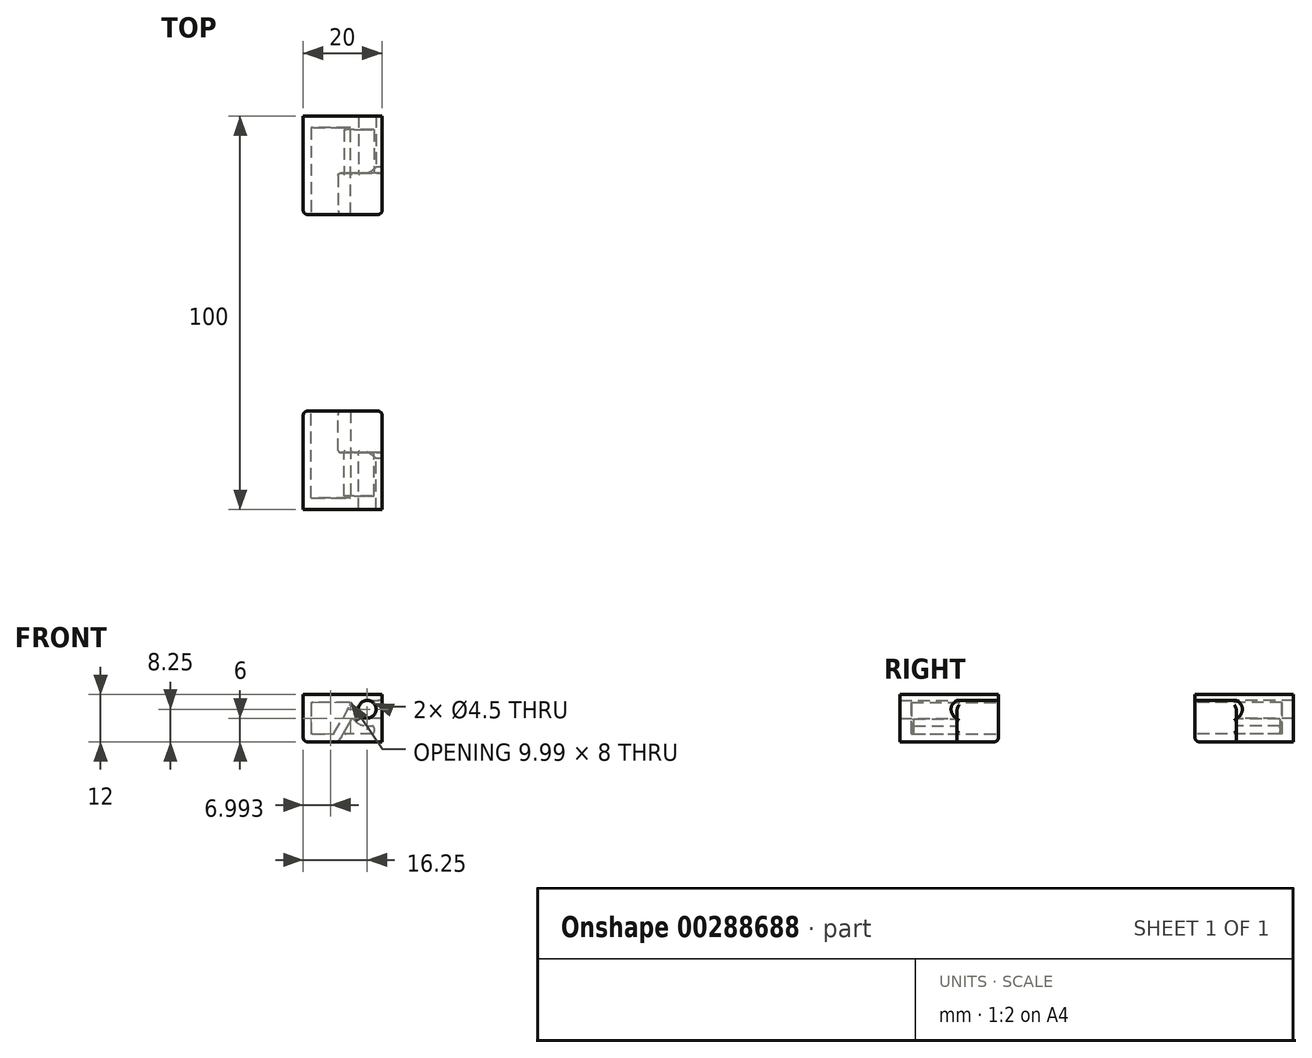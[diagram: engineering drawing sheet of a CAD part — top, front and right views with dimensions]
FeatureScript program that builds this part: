
annotation { "Feature Type Name" : "Feature", "Feature Type Description" : "" }
export const myFeature = defineFeature(function(context is Context, id is Id, definition is map)
    precondition{}
    {
        {
            var Q0;
            Q0=qCreatedBy(makeId("Front.planeOp"),FACE);
            var sketch = newSketch(context, id + "F0", { "sketchPlane" : qUnion([Q0])});
            skCircle(sketch, "E0", {"center": v(0, 0) * mm, "radius": 2.25 * mm});
            skLineSegment(sketch, "E1.bottom", {"start": v(-16.25, 3.75) * mm, "end": v(3.75, 3.75) * mm});
            skLineSegment(sketch, "E1.top", {"start": v(-16.25, -8.25) * mm, "end": v(3.75, -8.25) * mm});
            skLineSegment(sketch, "E1.left", {"start": v(-16.25, 3.75) * mm, "end": v(-16.25, -8.25) * mm});
            skLineSegment(sketch, "E1.right", {"start": v(3.75, 3.75) * mm, "end": v(3.75, -8.25) * mm});
            skSolve(sketch);
        }
        {
            var Q0;
            Q0=makeQuery(id+"F0.imprint","IMPRINT",FACE,{"disambiguationData":[TD([[makeQuery(id+"F0.imprint","IMPRINT",EDGE,{"derivedFrom":sQuery(id+"F0.wireOp",EDGE,"E0")}),-1.0]])]});
            extrude(context, id + "F1", {"entities" : qUnion([Q0]), "oppositeDirection" : true, "depth" : 25 * mm});
        }
        {
            var Q0;
            Q0=makeQuery(id+"F1.opExtrude","CAP_FACE",FACE,{"disambiguationData":[OSD([sQuery(id+"F0.wireOp",EDGE,"E0"),sQuery(id+"F0.wireOp",EDGE,"E1.bottom"),sQuery(id+"F0.wireOp",EDGE,"E1.top"),sQuery(id+"F0.wireOp",EDGE,"E1.left"),sQuery(id+"F0.wireOp",EDGE,"E1.right")])],"isStart":true});
            var sketch = newSketch(context, id + "F2", { "sketchPlane" : qUnion([Q0])});
            skLineSegment(sketch, "E2", {"start": v(0, 2.25) * mm, "end": v(3.75, 2.25) * mm});
            skLineSegment(sketch, "E3", {"start": v(-1.95, 1.13) * mm, "end": v(-7.36, -8.25) * mm});
            skArc(sketch, "E4.0", {"start": v(0, 2.25) * mm, "mid": v(-1.13, 1.95) * mm, "end": v(-1.95, 1.13) * mm});
            skPoint(sketch, "E5.orphan", {"position": v(3.75, -8.25) * mm});
            skLineSegment(sketch, "E6.0", {"start": v(-7.36, -8.25) * mm, "end": v(3.75, -8.25) * mm});
            skLineSegment(sketch, "E7.0", {"start": v(3.75, 2.25) * mm, "end": v(3.75, -8.25) * mm});
            skPoint(sketch, "E8.orphan", {"position": v(3.75, 3.75) * mm});
            skPoint(sketch, "E9.orphan", {"position": v(-16.25, -8.25) * mm});
            skSolve(sketch);
        }
        {
            var Q0;
            Q0 = qSketchRegion(id + "F2", true);
            extrude(context, id + "F3", {"entities" : qUnion([Q0]), "operationType" : NewBodyOperationType.REMOVE, "oppositeDirection" : true, "depth" : 10.5 * mm});
        }
        {
            var Q0;
            Q0=makeQuery(id+"F1.opExtrude","CAP_FACE",FACE,{"disambiguationData":[OSD([sQuery(id+"F0.wireOp",EDGE,"E0"),sQuery(id+"F0.wireOp",EDGE,"E1.bottom"),sQuery(id+"F0.wireOp",EDGE,"E1.top"),sQuery(id+"F0.wireOp",EDGE,"E1.left"),sQuery(id+"F0.wireOp",EDGE,"E1.right")])],"isStart":true});
            var sketch = newSketch(context, id + "F4", { "sketchPlane" : qUnion([Q0])});
            skLineSegment(sketch, "E10", {"start": v(-14.25, 1.75) * mm, "end": v(-14.25, -6.25) * mm});
            skLineSegment(sketch, "E11", {"start": v(-14.25, -6.25) * mm, "end": v(-8.52, -6.25) * mm});
            skLineSegment(sketch, "E12", {"start": v(-8.52, -6.25) * mm, "end": v(-3.9, 1.75) * mm});
            skLineSegment(sketch, "E13", {"start": v(-3.9, 1.75) * mm, "end": v(-14.25, 1.75) * mm});
            skSolve(sketch);
        }
        {
            var Q0;
            Q0 = qSketchRegion(id + "F4", true);
            extrude(context, id + "F5", {"entities" : qUnion([Q0]), "operationType" : NewBodyOperationType.REMOVE, "oppositeDirection" : true, "depth" : 22 * mm});
        }
        {
            var Q0;
            Q0=makeQuery(id+"F3.boolean.opBoolean","COPY",FACE,{"derivedFrom":makeQuery(id+"F3.opExtrude","CAP_FACE",FACE,{"disambiguationData":[OSD([sQuery(id+"F2.wireOp",EDGE,"E2"),sQuery(id+"F2.wireOp",EDGE,"E3"),sQuery(id+"F2.wireOp",EDGE,"E4.0"),sQuery(id+"F2.wireOp",EDGE,"E6.0"),sQuery(id+"F2.wireOp",EDGE,"E7.0")])],"isStart":false})});
            var sketch = newSketch(context, id + "F6", { "sketchPlane" : qUnion([Q0])});
            skLineSegment(sketch, "E14.0.1", {"start": v(-3.75, -2) * mm, "end": v(-6.2, -6.25) * mm});
            skArc(sketch, "E15.trimOffspring", {"start": v(-3.75, -2) * mm, "mid": v(-2.19, -3.64) * mm, "end": v(0, -4.25) * mm});
            skPoint(sketch, "E14.0.0.start.orphan", {"position": v(0, 2.25) * mm});
            skPoint(sketch, "E14.0.4.start.orphan", {"position": v(3.75, 2.25) * mm});
            skPoint(sketch, "E16.orphan", {"position": v(-1.95, 1.13) * mm});
            skPoint(sketch, "E17.0.2.end.orphan", {"position": v(3.75, -8.25) * mm});
            skPoint(sketch, "E17.0.2.start.orphan", {"position": v(-7.36, -8.25) * mm});
            skLineSegment(sketch, "E18", {"start": v(0, -4.25) * mm, "end": v(1.75, -4.25) * mm});
            skLineSegment(sketch, "E19", {"start": v(1.75, -4.25) * mm, "end": v(1.75, -6.25) * mm});
            skLineSegment(sketch, "E20", {"start": v(1.75, -6.25) * mm, "end": v(-6.2, -6.25) * mm});
            skSolve(sketch);
        }
        {
            var Q0;
            Q0 = qSketchRegion(id + "F6", true);
            extrude(context, id + "F7", {"entities" : qUnion([Q0]), "operationType" : NewBodyOperationType.REMOVE, "oppositeDirection" : true, "depth" : 11 * mm});
        }
        {
            var Q0;
            Q0=qCreatedBy(makeId("Right.planeOp"),FACE);
            var sketch = newSketch(context, id + "F8", { "sketchPlane" : qUnion([Q0])});
            skArc(sketch, "E21", {"start": v(10.5, -2.25) * mm, "mid": v(12, 0) * mm, "end": v(10.5, 2.25) * mm});
            skLineSegment(sketch, "E22", {"start": v(10.5, 2.25) * mm, "end": v(10.5, -2.25) * mm});
            skSolve(sketch);
        }
        {
            var Q0;
            Q0 = qSketchRegion(id + "F8", true);
            extrude(context, id + "F9", {"entities" : qUnion([Q0]), "operationType" : NewBodyOperationType.REMOVE, "endBound" : BoundingType.THROUGH_ALL, "depth" : 25 * mm});
        }
        {
            var Q0;
            Q0=makeQuery(id+"F1.opExtrude","SWEPT_FACE",FACE,{"disambiguationData":[OSD([sQuery(id+"F0.wireOp",EDGE,"E0")])]});
            var Q1;
            Q1=makeQuery(id+"F3.boolean.opBoolean","COPY",EDGE,{"derivedFrom":makeQuery(id+"F3.opExtrude","CAP_EDGE",EDGE,{"disambiguationData":[OSD([sQuery(id+"F2.wireOp",EDGE,"E3")])],"isStart":true})});
            cPlane(context, id + "F10", {"entities" : qUnion([Q0, Q1]), "cplaneType" : CPlaneType.LINE_ANGLE, "offset" : 25 * mm, "angle" : 90 * degree, "oppositeDirection" : true, "width" : 150 * mm, "height" : 150 * mm});
        }
        {
            var Q0;
            Q0=qCreatedBy(id+"F10.planeOp",FACE);
            var sketch = newSketch(context, id + "F11", { "sketchPlane" : qUnion([Q0])});
            skLineSegment(sketch, "E23", {"start": v(0, 1.94) * mm, "end": v(0, -15.89) * mm, "construction": true});
            skArc(sketch, "E24", {"start": v(-2.25, -10.5) * mm, "mid": v(0, -12) * mm, "end": v(2.25, -10.5) * mm});
            skLineSegment(sketch, "E25", {"start": v(-2.25, -10.5) * mm, "end": v(2.25, -10.5) * mm});
            skSolve(sketch);
        }
        {
            var Q0;
            Q0=makeQuery(id+"F11.imprint","IMPRINT",FACE,{"disambiguationData":[TD([[makeQuery(id+"F11.imprint","IMPRINT",EDGE,{"derivedFrom":sQuery(id+"F11.wireOp",EDGE,"E24")}),1.0]])]});
            extrude(context, id + "F12", {"entities" : qUnion([Q0]), "operationType" : NewBodyOperationType.REMOVE, "endBound" : BoundingType.THROUGH_ALL, "depth" : 25 * mm});
        }
        {
            var Q0;
            Q0=makeQuery(id+"F5.boolean.opBoolean","COPY",EDGE,{"derivedFrom":makeQuery(id+"F5.opExtrude","SWEPT_EDGE",EDGE,{"disambiguationData":[OSD([sQuery(id+"F4.wireOp",EDGE,"E10"),sQuery(id+"F4.wireOp",EDGE,"E13")])]})});
            var Q1;
            Q1=makeQuery(id+"F5.boolean.opBoolean","COPY",EDGE,{"derivedFrom":makeQuery(id+"F5.opExtrude","SWEPT_EDGE",EDGE,{"disambiguationData":[OSD([sQuery(id+"F4.wireOp",EDGE,"E12"),sQuery(id+"F4.wireOp",EDGE,"E13")])]})});
            var Q2;
            Q2=makeQuery(id+"F5.boolean.opBoolean","COPY",EDGE,{"derivedFrom":makeQuery(id+"F5.opExtrude","SWEPT_EDGE",EDGE,{"disambiguationData":[OSD([sQuery(id+"F4.wireOp",EDGE,"E10"),sQuery(id+"F4.wireOp",EDGE,"E11")])]})});
            var Q3;
            Q3=makeQuery(id+"F5.boolean.opBoolean","COPY",EDGE,{"derivedFrom":makeQuery(id+"F5.opExtrude","SWEPT_EDGE",EDGE,{"disambiguationData":[OSD([sQuery(id+"F4.wireOp",EDGE,"E11"),sQuery(id+"F4.wireOp",EDGE,"E12")])]})});
            var Q4;
            Q4=makeQuery(id+"F7.boolean.opBoolean","COPY",EDGE,{"derivedFrom":makeQuery(id+"F7.opExtrude","SWEPT_EDGE",EDGE,{"disambiguationData":[OSD([sQuery(id+"F2.wireOp",EDGE,"E3"),sQuery(id+"F6.wireOp",EDGE,"E14.0.1"),sQuery(id+"F6.wireOp",EDGE,"CT78Zgtt-ATp1-XAIS-9uUU-WfGeracGuKnf")])]})});
            var Q5;
            Q5=makeQuery(id+"F7.boolean.opBoolean","COPY",EDGE,{"derivedFrom":makeQuery(id+"F7.opExtrude","SWEPT_EDGE",EDGE,{"disambiguationData":[OSD([sQuery(id+"F2.wireOp",EDGE,"E3"),sQuery(id+"F6.wireOp",EDGE,"E14.0.1"),sQuery(id+"F6.wireOp",EDGE,"E15.trimOffspring")])]})});
            var Q6;
            Q6=makeQuery(id+"F7.boolean.opBoolean","COPY",EDGE,{"derivedFrom":makeQuery(id+"F7.opExtrude","SWEPT_EDGE",EDGE,{"disambiguationData":[OSD([sQuery(id+"F6.wireOp",EDGE,"E19"),sQuery(id+"F6.wireOp",EDGE,"E20")])]})});
            var Q7;
            Q7=makeQuery(id+"F7.boolean.opBoolean","COPY",EDGE,{"derivedFrom":makeQuery(id+"F7.opExtrude","SWEPT_EDGE",EDGE,{"disambiguationData":[OSD([sQuery(id+"F6.wireOp",EDGE,"E18"),sQuery(id+"F6.wireOp",EDGE,"E19")])]})});
            var Q8;
            {var subQ0=sQuery(id+"F11.wireOp",EDGE,"E24");var subQ1=sQuery(id+"F11.wireOp",EDGE,"E25");Q8=makeQuery(id+"F12.boolean.opBoolean","COPY",EDGE,{"disambiguationData":[TD([makeQuery(id+"F1.opExtrude","SWEPT_FACE",FACE,{"disambiguationData":[OSD([sQuery(id+"F0.wireOp",EDGE,"E1.top")])]})])],"derivedFrom":makeQuery(id+"F12.opExtrude","SWEPT_EDGE",EDGE,{"disambiguationData":[OSD([subQ0,subQ1]),TDD([makeQuery(id+"F11.imprint","INTERSECT",VERTEX,{"disambiguationData":[OD(1.0)],"derivedFrom":[subQ0,subQ1]})])]})});}
            var Q9;
            {var subQ0=sQuery(id+"F11.wireOp",EDGE,"E24");var subQ1=sQuery(id+"F11.wireOp",EDGE,"E25");Q9=makeQuery(id+"F12.boolean.opBoolean","COPY",EDGE,{"disambiguationData":[TD([makeQuery(id+"F7.boolean.opBoolean","COPY",FACE,{"derivedFrom":makeQuery(id+"F7.opExtrude","SWEPT_FACE",FACE,{"disambiguationData":[OSD([sQuery(id+"F6.wireOp",EDGE,"E18")])]})})])],"derivedFrom":makeQuery(id+"F12.opExtrude","SWEPT_EDGE",EDGE,{"disambiguationData":[OSD([subQ0,subQ1]),TDD([makeQuery(id+"F11.imprint","INTERSECT",VERTEX,{"disambiguationData":[OD(1.0)],"derivedFrom":[subQ0,subQ1]})])]})});}
            var Q10;
            {var subQ0=sQuery(id+"F8.wireOp",EDGE,"E22");var subQ1=sQuery(id+"F8.wireOp",EDGE,"E21");Q10=makeQuery(id+"F9.boolean.opBoolean","COPY",EDGE,{"derivedFrom":makeQuery(id+"F9.opExtrude","SWEPT_EDGE",EDGE,{"disambiguationData":[OSD([subQ1,subQ0]),TDD([makeQuery(id+"F8.imprint","INTERSECT",VERTEX,{"disambiguationData":[OD(0.0)],"derivedFrom":[subQ1,subQ0]})])]})});}
            var Q11;
            {var subQ0=sQuery(id+"F11.wireOp",EDGE,"E25");var subQ1=sQuery(id+"F11.wireOp",EDGE,"E24");var subQ2=sQuery(id+"F2.wireOp",EDGE,"E3");Q11=makeQuery(id+"F12.boolean.opBoolean","MERGE",EDGE,{"derivedFrom":[makeQuery(id+"F7.boolean.opBoolean","SPLIT",EDGE,{"disambiguationData":[TD([makeQuery(id+"F1.opExtrude","SWEPT_FACE",FACE,{"disambiguationData":[OSD([sQuery(id+"F0.wireOp",EDGE,"E1.top")])]})])],"derivedFrom":makeQuery(id+"F3.boolean.opBoolean","COPY",EDGE,{"derivedFrom":makeQuery(id+"F3.opExtrude","CAP_EDGE",EDGE,{"disambiguationData":[OSD([subQ2])],"isStart":false})})}),makeQuery(id+"F12.opExtrude","SWEPT_EDGE",EDGE,{"disambiguationData":[OSD([subQ1,subQ0]),TDD([makeQuery(id+"F11.imprint","INTERSECT",VERTEX,{"disambiguationData":[OD(0.0)],"derivedFrom":[subQ1,subQ0]})])]})]});}
            var Q12;
            {var subQ0=sQuery(id+"F11.wireOp",EDGE,"E25");var subQ1=sQuery(id+"F11.wireOp",EDGE,"E24");var subQ2=sQuery(id+"F2.wireOp",EDGE,"E3");Q12=makeQuery(id+"F12.boolean.opBoolean","MERGE",EDGE,{"derivedFrom":[makeQuery(id+"F7.boolean.opBoolean","SPLIT",EDGE,{"disambiguationData":[TD([makeQuery(id+"F1.opExtrude","SWEPT_FACE",FACE,{"disambiguationData":[OSD([sQuery(id+"F0.wireOp",EDGE,"E0")])]})])],"derivedFrom":makeQuery(id+"F3.boolean.opBoolean","COPY",EDGE,{"derivedFrom":makeQuery(id+"F3.opExtrude","CAP_EDGE",EDGE,{"disambiguationData":[OSD([subQ2])],"isStart":false})})}),makeQuery(id+"F12.opExtrude","SWEPT_EDGE",EDGE,{"disambiguationData":[OSD([subQ1,subQ0]),TDD([makeQuery(id+"F11.imprint","INTERSECT",VERTEX,{"disambiguationData":[OD(0.0)],"derivedFrom":[subQ1,subQ0]})])]})]});}
            var Q13;
            {var subQ0=sQuery(id+"F8.wireOp",EDGE,"E22");var subQ1=sQuery(id+"F8.wireOp",EDGE,"E21");Q13=makeQuery(id+"F9.boolean.opBoolean","MERGE",EDGE,{"derivedFrom":[makeQuery(id+"F3.boolean.opBoolean","COPY",EDGE,{"derivedFrom":makeQuery(id+"F3.opExtrude","CAP_EDGE",EDGE,{"disambiguationData":[OSD([sQuery(id+"F2.wireOp",EDGE,"E2")])],"isStart":false})}),makeQuery(id+"F9.opExtrude","SWEPT_EDGE",EDGE,{"disambiguationData":[OSD([subQ1,subQ0]),TDD([makeQuery(id+"F8.imprint","INTERSECT",VERTEX,{"disambiguationData":[OD(1.0)],"derivedFrom":[subQ1,subQ0]})])]})]});}
            fillet(context, id + "F13", {"entities" : qUnion([Q0, Q1, Q2, Q3, Q4, Q5, Q6, Q7, Q8, Q9, Q10, Q11, Q12, Q13]), "radius" : 0.5 * mm, "allowEdgeOverflow" : false});
        }
        {
            var Q0;
            Q0=makeQuery(id+"F1.opExtrude","CAP_EDGE",EDGE,{"disambiguationData":[OSD([sQuery(id+"F0.wireOp",EDGE,"E1.right")])],"isStart":true});
            var Q1;
            Q1=makeQuery(id+"F1.opExtrude","CAP_EDGE",EDGE,{"disambiguationData":[OSD([sQuery(id+"F0.wireOp",EDGE,"E1.left")])],"isStart":true});
            var Q2;
            Q2=makeQuery(id+"F1.opExtrude","SWEPT_EDGE",EDGE,{"disambiguationData":[OSD([sQuery(id+"F0.wireOp",EDGE,"E1.top"),sQuery(id+"F0.wireOp",EDGE,"E1.left")])]});
            var Q3;
            Q3=makeQuery(id+"F1.opExtrude","CAP_EDGE",EDGE,{"disambiguationData":[OSD([sQuery(id+"F0.wireOp",EDGE,"E1.top")])],"isStart":true});
            var Q4;
            Q4=makeQuery(id+"F3.boolean.opBoolean","COPY",EDGE,{"derivedFrom":makeQuery(id+"F3.opExtrude","CAP_EDGE",EDGE,{"disambiguationData":[OSD([sQuery(id+"F2.wireOp",EDGE,"E3")])],"isStart":true})});
            fillet(context, id + "F14", {"entities" : qUnion([Q0, Q1, Q2, Q3, Q4]), "radius" : 1 * mm, "tangentPropagation" : true, "allowEdgeOverflow" : false});
        }
        {
            var Q0;
            Q0=qCreatedBy(makeId("Front.planeOp"),FACE);
            cPlane(context, id + "F15", {"entities" : qUnion([Q0]), "cplaneType" : CPlaneType.OFFSET, "offset" : 25 * mm, "width" : 150 * mm, "height" : 150 * mm});
        }
        {
            var Q0;
            Q0=makeQuery(id+"F1.opExtrude","SWEPT_BODY",BODY,{"disambiguationData":[OSD([sQuery(id+"F0.wireOp",EDGE,"E0"),sQuery(id+"F0.wireOp",EDGE,"E1.bottom"),sQuery(id+"F0.wireOp",EDGE,"E1.top"),sQuery(id+"F0.wireOp",EDGE,"E1.left"),sQuery(id+"F0.wireOp",EDGE,"E1.right")])]});
            var Q1;
            Q1=qCreatedBy(id+"F15.planeOp",FACE);
            mirror(context, id + "F16", {"entities" : qUnion([Q0]), "mirrorPlane" : qUnion([Q1])});
        }
    });
